# Revit family: P500208-009
name_source: partatom
category: Lighting Fixtures
revit_build: Autodesk Revit 2014 (Build: 20130308_1515(x64)
units: mm (PartAtom-declared; Revit-internal decimal feet)

## types (1)
- P500230-031
    Apparent Load = 60 VA
    Assembly Code = D5020200
    Color Filter = 16777215
    Connector Description = Lighting Connector
    Default Elevation = 48"
    Description = Introduce a pop of personality into your home with this pendant. A round
ceiling plate coated in a black finish anchors the pendant in place as the
light source hangs below. A bottle-inspired clear glass shade adds a twist to
a simple industrial style that brings this light fixture’s vintage charm to the
forefront of your home’s lighting design.
    Diameter = 9 7/16"
    Dimming Lamp Color Temperature Shift = <None>
    Fixture distribution = Direct
    Glass = Hubbell - Glass
    Gold = Hubbell - Gold
    Height = 15 1/2"
    Housing Material = Paint - Hubbell - Textured Camera Black
    Lamp = A-19
    Load Classification = Lighting
    Manufacturer = Progress Lighting
    Model = P500230-031
    Photometric Web File = generic
    Power Factor = 1
    Product Documentation Link = https://hubbellcdn.com
    Product Link = https://www.hubbell.com
    Specifications = A round ceiling plate coated in a black finish anchors the pendant in place as the light source
hangs below.
• A bottle-inspired clear glass shade adds a twist to a simple industrial style that brings this
light fixture’s vintage charm to the forefront of your home’s lighting design.
• Introduce a pop of personality into your home with this pendant.
• Ideal for any foyer, kitchen, or dining room.
• Perfect for transitional, farmhouse, or coastal settings.
• Measures 7.43-inch width by 17.18-inch height.
• Uses one medium base bulb that is sold separately (60w max - LED or incandescent).
• Able to be fully dimmable with dimmable bulbs.
• Includes installation instructions and mounting hardware.
• Progress Lighting products are designed for exceptional quality, reliability, and functionality
    Tilt Angle = 60.00°
    URL = https://www.hubbell.com
    Voltage = 120 V
    Warranty = 5 years Warranty
    Wattage Comments = 60W
    Watts = 60 W
    White = Paint - Hubbell - Matte White

## geometry (parser evidence)
native form markers: Sweep x6
no freeform markers — native parametric forms only
